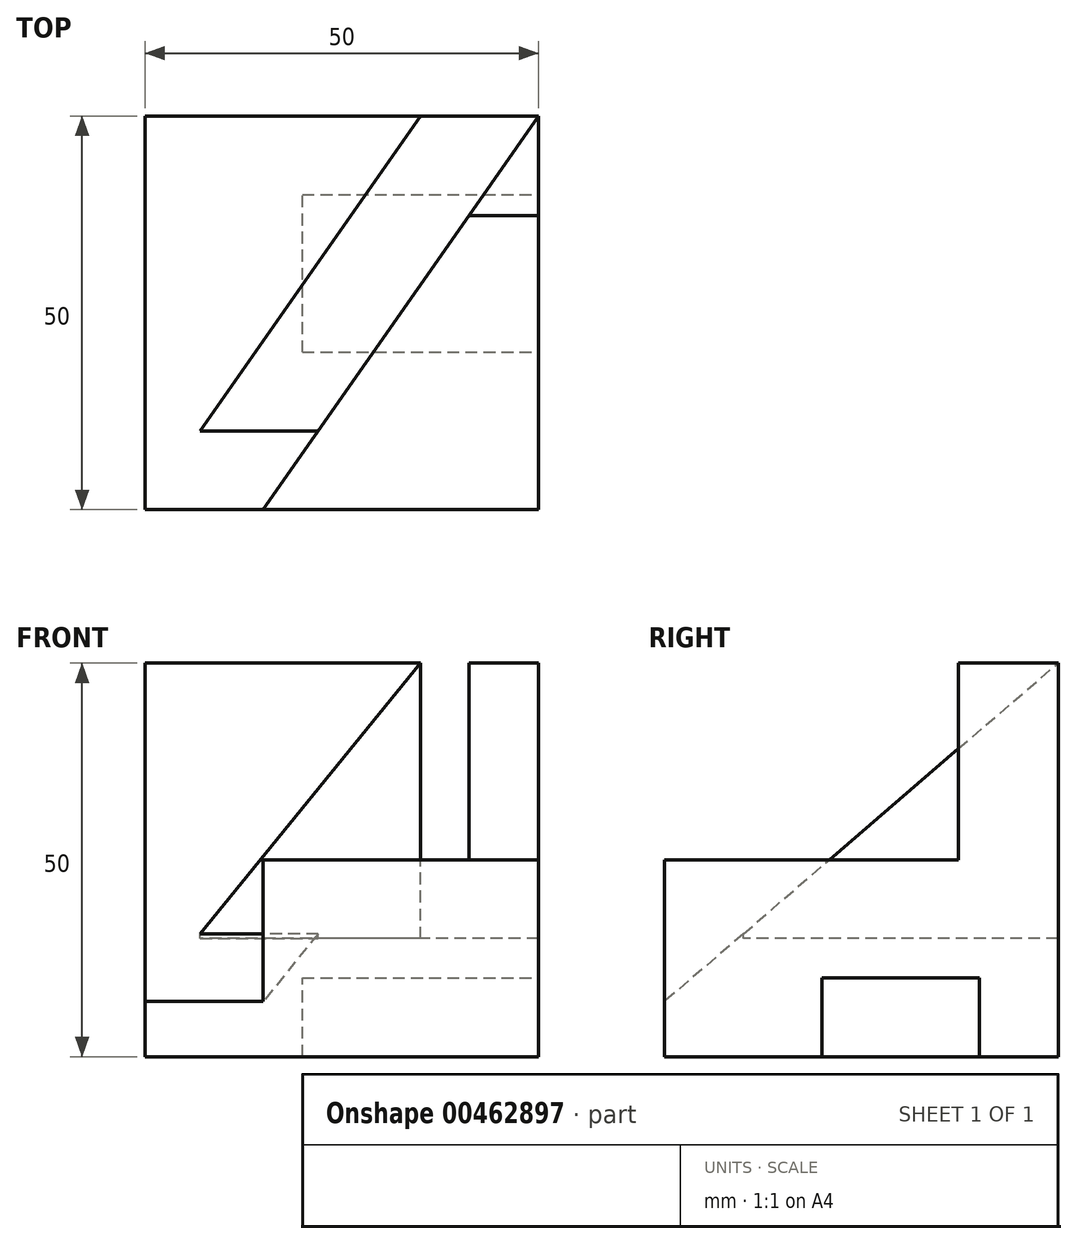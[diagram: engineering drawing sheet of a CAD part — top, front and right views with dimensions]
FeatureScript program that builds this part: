
annotation { "Feature Type Name" : "Feature", "Feature Type Description" : "" }
export const myFeature = defineFeature(function(context is Context, id is Id, definition is map)
    precondition{}
    {
        {
            var Q0;
            Q0=qCreatedBy(makeId("Front.planeOp"),FACE);
            var sketch = newSketch(context, id + "F0", { "sketchPlane" : qUnion([Q0])});
            skLineSegment(sketch, "E0.bottom", {"start": v(0, 0) * mm, "end": v(-50, 0) * mm});
            skLineSegment(sketch, "E0.top", {"start": v(0, 50) * mm, "end": v(-50, 50) * mm});
            skLineSegment(sketch, "E0.left", {"start": v(0, 0) * mm, "end": v(0, 50) * mm});
            skLineSegment(sketch, "E0.right", {"start": v(-50, 0) * mm, "end": v(-50, 50) * mm});
            skSolve(sketch);
        }
        {
            var Q0;
            Q0 = qSketchRegion(id + "F0", true);
            extrude(context, id + "F1", {"entities" : qUnion([Q0]), "depth" : 50 * mm});
        }
        {
            var Q0;
            Q0=makeQuery(id+"F1.opExtrude","SWEPT_FACE",FACE,{"disambiguationData":[OSD([sQuery(id+"F0.wireOp",EDGE,"E0.top")])]});
            var sketch = newSketch(context, id + "F2", { "sketchPlane" : qUnion([Q0])});
            skLineSegment(sketch, "E1", {"start": v(0, 0) * mm, "end": v(-35, -50) * mm});
            skLineSegment(sketch, "E2", {"start": v(-35, -50) * mm, "end": v(-50, -50) * mm});
            skLineSegment(sketch, "E3", {"start": v(-50, -50) * mm, "end": v(-50, 0) * mm});
            skLineSegment(sketch, "E4", {"start": v(-50, 0) * mm, "end": v(0, 0) * mm});
            skSolve(sketch);
        }
        {
            var Q0;
            Q0=makeQuery(id+"F2.imprint","IMPRINT",FACE,{"disambiguationData":[TD([[makeQuery(id+"F2.imprint","IMPRINT",EDGE,{"derivedFrom":sQuery(id+"F2.wireOp",EDGE,"E1")}),-1.0]])]});
            extrude(context, id + "F3", {"entities" : qUnion([Q0]), "operationType" : NewBodyOperationType.REMOVE, "oppositeDirection" : true, "depth" : 43 * mm});
        }
        {
            var Q0;
            Q0=makeQuery(id+"F1.opExtrude","SWEPT_FACE",FACE,{"disambiguationData":[OSD([sQuery(id+"F0.wireOp",EDGE,"E0.top")])]});
            var sketch = newSketch(context, id + "F4", { "sketchPlane" : qUnion([Q0])});
            skLineSegment(sketch, "E5", {"start": v(0, 0) * mm, "end": v(-8.85, -12.64) * mm});
            skLineSegment(sketch, "E6", {"start": v(-8.85, -12.64) * mm, "end": v(0, -12.64) * mm});
            skLineSegment(sketch, "E7", {"start": v(0, -12.64) * mm, "end": v(0, 0) * mm});
            skSolve(sketch);
        }
        {
            var Q0;
            {var subQ0=sQuery(id+"F4.wireOp",EDGE,"E6");Q0=makeQuery(id+"F4.imprint","IMPRINT",FACE,{"disambiguationData":[TD([[makeQuery(id+"F4.imprint","IMPRINT",EDGE,{"derivedFrom":subQ0}),-1.0]])]});}
            extrude(context, id + "F5", {"entities" : qUnion([Q0]), "operationType" : NewBodyOperationType.REMOVE, "oppositeDirection" : true, "depth" : 25 * mm});
        }
        {
            var Q0;
            Q0=makeQuery(id+"F3.boolean.opBoolean","COPY",FACE,{"derivedFrom":makeQuery(id+"F3.opExtrude","CAP_FACE",FACE,{"disambiguationData":[OSD([sQuery(id+"F2.wireOp",EDGE,"E1"),sQuery(id+"F2.wireOp",EDGE,"E2"),sQuery(id+"F2.wireOp",EDGE,"E3"),sQuery(id+"F2.wireOp",EDGE,"E4")])],"isStart":false})});
            var sketch = newSketch(context, id + "F6", { "sketchPlane" : qUnion([Q0])});
            skLineSegment(sketch, "E8", {"start": v(-50, -50) * mm, "end": v(-35, -50) * mm});
            skLineSegment(sketch, "E9", {"start": v(-35, -50) * mm, "end": v(-50, -71.43) * mm});
            skLineSegment(sketch, "E10", {"start": v(-50, -71.43) * mm, "end": v(-50, -50) * mm});
            skSolve(sketch);
        }
        {
            var Q0;
            Q0=sQuery(id+"F2.wireOp",VERTEX,"E1.start");
            var Q1;
            Q1=sQuery(id+"F2.wireOp",VERTEX,"E4.start");
            var Q2;
            Q2=sQuery(id+"F6.wireOp",VERTEX,"E9.end");
            cPlane(context, id + "F7", {"entities" : qUnion([Q0, Q1, Q2]), "cplaneType" : CPlaneType.THREE_POINT, "offset" : 25 * mm, "width" : 150 * mm, "height" : 150 * mm});
        }
        {
            var Q0;
            Q0=makeQuery(id+"F6.imprint","IMPRINT",FACE,{"disambiguationData":[TD([[makeQuery(id+"F6.imprint","IMPRINT",EDGE,{"derivedFrom":sQuery(id+"F6.wireOp",EDGE,"E8")}),-1.0]])]});
            var Q1;
            Q1=qCreatedBy(id+"F7.planeOp",FACE);
            extrude(context, id + "F8", {"entities" : qUnion([Q0]), "operationType" : NewBodyOperationType.ADD, "endBound" : BoundingType.UP_TO_SURFACE, "endBoundEntityFace" : qUnion([Q1]), "depth" : 25 * mm});
        }
        {
            var Q0;
            Q0=makeQuery(id+"F2.imprint","IMPRINT",FACE,{"disambiguationData":[TD([[makeQuery(id+"F2.imprint","IMPRINT",EDGE,{"derivedFrom":sQuery(id+"F2.wireOp",EDGE,"E1")}),-1.0]])]});
            var sketch = newSketch(context, id + "F9", { "sketchPlane" : qUnion([Q0])});
            skLineSegment(sketch, "E11", {"start": v(0, 0) * mm, "end": v(-15, 0) * mm});
            skLineSegment(sketch, "E12", {"start": v(-43, -40) * mm, "end": v(-28, -40) * mm});
            skLineSegment(sketch, "E13", {"start": v(-15, 0) * mm, "end": v(-43, -40) * mm});
            skLineSegment(sketch, "E14", {"start": v(0, 0) * mm, "end": v(-28, -40) * mm});
            skSolve(sketch);
        }
        {
            var Q0;
            {var subQ0=sQuery(id+"F9.wireOp",EDGE,"E11");Q0=makeQuery(id+"F9.imprint","IMPRINT",FACE,{"disambiguationData":[TD([[makeQuery(id+"F9.imprint","IMPRINT",EDGE,{"derivedFrom":subQ0}),1.0]])]});}
            extrude(context, id + "F10", {"entities" : qUnion([Q0]), "operationType" : NewBodyOperationType.REMOVE, "oppositeDirection" : true, "depth" : 35 * mm});
        }
        {
            var Q0;
            Q0=makeQuery(id+"F8.boolean.opBoolean","MERGE",FACE,{"derivedFrom":[makeQuery(id+"F1.opExtrude","SWEPT_FACE",FACE,{"disambiguationData":[OSD([sQuery(id+"F0.wireOp",EDGE,"E0.right")])]}),makeQuery(id+"F8.opExtrude","SWEPT_FACE",FACE,{"disambiguationData":[OSD([sQuery(id+"F2.wireOp",EDGE,"E3")])]})]});
            var sketch = newSketch(context, id + "F11", { "sketchPlane" : qUnion([Q0])});
            skLineSegment(sketch, "E15", {"start": v(0, 50) * mm, "end": v(0, 7) * mm});
            skLineSegment(sketch, "E16", {"start": v(0, 7) * mm, "end": v(50, 7) * mm});
            skLineSegment(sketch, "E17", {"start": v(50, 7) * mm, "end": v(0, 50) * mm});
            skSolve(sketch);
        }
        {
            var Q0;
            {var subQ0=sQuery(id+"F11.wireOp",EDGE,"E17");Q0=makeQuery(id+"F11.imprint","IMPRINT",FACE,{"disambiguationData":[TD([[makeQuery(id+"F11.imprint","IMPRINT",EDGE,{"derivedFrom":subQ0}),-1.0]])]});}
            var Q1;
            {var subQ0=sQuery(id+"F2.wireOp",EDGE,"E1");Q1=makeQuery(id+"F8.boolean.opBoolean","SPLIT",FACE,{"disambiguationData":[TD([makeQuery(id+"F8.opExtrude","SWEPT_FACE",FACE,{"disambiguationData":[OSD([sQuery(id+"F6.wireOp",EDGE,"E8")])]})])],"derivedFrom":makeQuery(id+"F3.boolean.opBoolean","COPY",FACE,{"derivedFrom":makeQuery(id+"F3.opExtrude","SWEPT_FACE",FACE,{"disambiguationData":[OSD([subQ0])]})})});}
            extrude(context, id + "F12", {"entities" : qUnion([Q0]), "operationType" : NewBodyOperationType.REMOVE, "endBound" : BoundingType.UP_TO_SURFACE, "oppositeDirection" : true, "endBoundEntityFace" : qUnion([Q1]), "depth" : 25 * mm});
        }
        {
            var Q0;
            Q0=makeQuery(id+"F1.opExtrude","SWEPT_FACE",FACE,{"disambiguationData":[OSD([sQuery(id+"F0.wireOp",EDGE,"E0.left")])]});
            var sketch = newSketch(context, id + "F13", { "sketchPlane" : qUnion([Q0])});
            skLineSegment(sketch, "E18.bottom", {"start": v(-30, 0) * mm, "end": v(-10, 0) * mm});
            skLineSegment(sketch, "E18.top", {"start": v(-30, 10) * mm, "end": v(-10, 10) * mm});
            skLineSegment(sketch, "E18.left", {"start": v(-30, 0) * mm, "end": v(-30, 10) * mm});
            skLineSegment(sketch, "E18.right", {"start": v(-10, 0) * mm, "end": v(-10, 10) * mm});
            skSolve(sketch);
        }
        {
            var Q0;
            Q0 = qSketchRegion(id + "F13", true);
            extrude(context, id + "F14", {"entities" : qUnion([Q0]), "operationType" : NewBodyOperationType.REMOVE, "oppositeDirection" : true, "depth" : 30 * mm});
        }
    });
